# Revit family: Flushometer-Urinal_Touchless-KOHLER-MACH_WAVE-K-40UH00K20_1
name_source: partatom
category: Plumbing Fixtures
revit_build: Autodesk Revit 2017 (Build: 20160225_1515(x64)
units: mm (PartAtom-declared; Revit-internal decimal feet)

## family parameters
Cut with Voids When Loaded = No
Host = Face
OmniClass Number = 23.27.31.00
OmniClass Title = Valves
Part Type = Normal
Room Calculation Point = No
Round Connector Dimension = Use Diameter
Shared = No

## types (2) — shared parameters
ADA Compliant = No
Assembly Code = D2020
CW Connection = Yes
Cold Water Inlet = Cold Water Inlet
Cold Water Outlet = Cold Water Outlet
Date Modified = 02/11/2021
Default Elevation = 0"
Finish = Kohler-Metal-CP-Polished_Chrome
Flow Rate = 0 GPM
Flush Rate- GPF = 1.0 GPF
Flush Rate- LPF = 3.8 LPF
HW Connection = No
Hot Water Inlet = Hot Water Inlet
Manufacturer = KOHLER Co.
Master Format 2014 = 23 09 13.33
Master Format 2014 Name = Control Valves
Material = Premium Metal Construction
Pressure = 0.00 psi
Product Documentation Link = https://www.us.kohler.com
Product Name = MACH WAVE
Product Page URL = http://www.us.kohler.com
RF Height = 8 1/16"
RF Length = 2 1/2"
RF Width = 3 1/2"
URL = https://www.us.kohler.com
Vent Connection = No
Waste Connection = No
Waste Water Outlet = Waste Water Outlet
WaterSense Certified = No

## per-type parameters (varying)
| type | Connector Dia 1 | Connector Dia 2 | Description | Model | Type | With Accessories | Without Accessories |
| 1.0 GPF Flushometer, CP-Polished Chrome | 3/4" | 0" | HEC 1.0 GPF URINAL FLASH VALVE | K-40UH00K20-CP | 1 | Yes | No |
| 1.0 GPF Retrofit Flushometer, CP-Polished Chrome | 0" | 3/4" | HEC 1.0 GPF URINAL RETROFIT FLASH VALVE | K-40UH00K20-RF-CP | 2 | No | Yes |

## geometry (parser evidence)
native form markers: Sweep x5
no freeform markers — native parametric forms only
